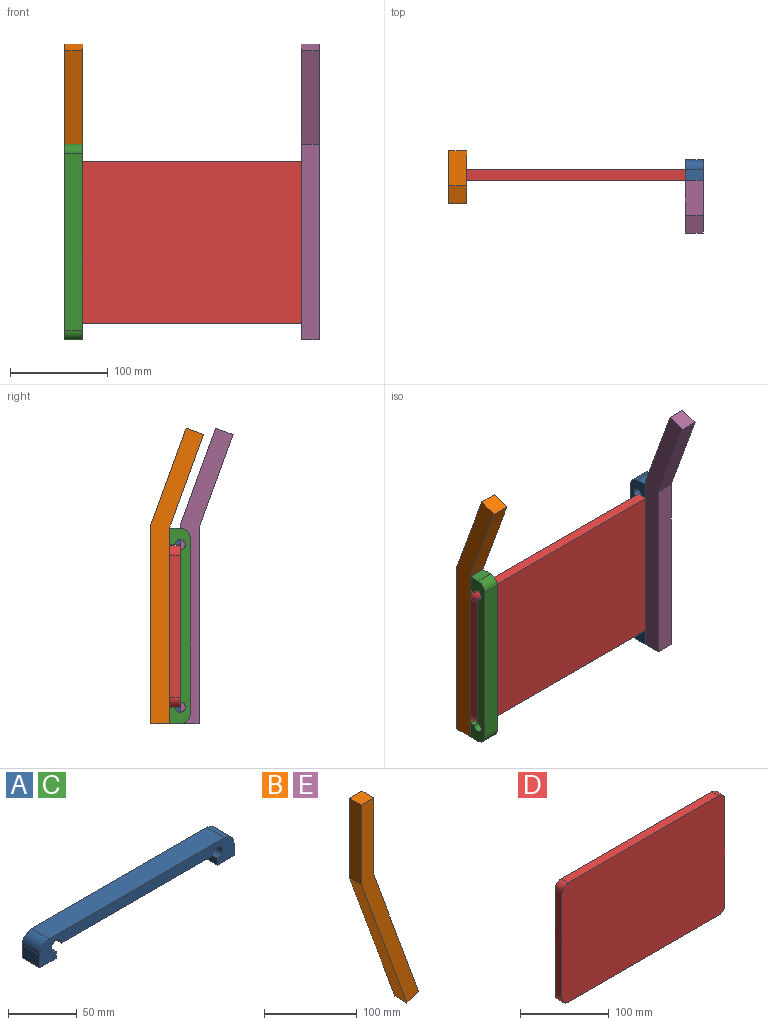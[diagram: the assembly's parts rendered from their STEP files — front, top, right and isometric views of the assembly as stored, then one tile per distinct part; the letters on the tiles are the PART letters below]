
ASSEMBLY  parts=5 mates=12
PART A: 14 faces, bbox 200x18.2x21 mm
  f0: plane 18.21x5.92mm, normal (1,0,0), area 107.8mm2, adj f6,f8,f9,f11
  f1: plane 155.84x18.21mm, normal (0,0,-1), area 2838.1mm2, adj f8,f9,f10,f11
  f2: plane 18.21x5.92mm, normal (-1,0,0), area 107.8mm2, adj f7,f8,f9,f10
  f3: plane 18.21x11.19mm, normal (1,0,0), area 203.8mm2, adj f7,f8,f9,f12
  f4: plane 180.38x18.21mm, normal (0,0,1), area 3285mm2, adj f8,f9,f12,f13
  f5: plane 18.21x11.19mm, normal (-1,0,0), area 203.8mm2, adj f6,f8,f9,f13
  f6: plane 18.21x17mm, normal (0,0,-1), area 309.6mm2, adj f0,f5,f8,f9
  f7: plane 18.21x17mm, normal (0,0,-1), area 309.6mm2, adj f2,f3,f8,f9
  f8: plane 200x21mm, normal (0,-1,0), area 2211.1mm2, adj f0,f1,f2,f3,f4,f5,f6,f7
  f9: plane 200x21mm, normal (0,1,0), area 2211.1mm2, adj f0,f1,f2,f3,f4,f5,f6,f7
  f10: cylinder r=5.08mm len=18.21mm, axis (0,-1,0), area 436mm2, adj f1,f2,f8,f9
  f11: cylinder r=5.08mm len=18.21mm, axis (0,-1,0), area 436mm2, adj f0,f1,f8,f9
  f12: cylinder r=9.81mm len=18.21mm, axis (0,1,0), area 280.7mm2, adj f3,f4,f8,f9
  f13: cylinder r=9.81mm len=18.21mm, axis (0,1,0), area 280.7mm2, adj f4,f5,f8,f9
PART B: 8 faces, bbox 87.5x18.2x296.1 mm
  f0: plane 187.94x68.4mm, normal (0.94,0,0.34), area 3642.4mm2, adj f1,f5,f6,f7
  f1: plane 101.6x18.21mm, normal (1,0,0), area 1850.3mm2, adj f0,f2,f6,f7
  f2: plane 19.05x18.21mm, normal (0,0,1), area 346.9mm2, adj f1,f3,f6,f7
  f3: plane 104.96x18.21mm, normal (-1,0,0), area 1911.5mm2, adj f2,f4,f6,f7
  f4: plane 191.1x69.55mm, normal (-0.94,0,-0.34), area 3703.5mm2, adj f3,f5,f6,f7
  f5: plane 18.21x17.9mm, normal (0.34,0,-0.94), area 346.9mm2, adj f0,f4,f6,f7
  f6: plane 296.05x87.45mm, normal (0,-1,0), area 5809.5mm2, adj f0,f1,f2,f3,f4,f5
  f7: plane 296.05x87.45mm, normal (0,1,0), area 5809.5mm2, adj f0,f1,f2,f3,f4,f5
PART C: same geometry as A
PART D: 10 faces, bbox 260x11.1x165 mm
  f0: plane 240x11.1mm, normal (0,0,-1), area 2664mm2, adj f4,f5,f6,f9
  f1: plane 145x11.1mm, normal (1,0,0), area 1609.5mm2, adj f4,f5,f6,f7
  f2: plane 240x11.1mm, normal (0,0,1), area 2664mm2, adj f4,f5,f7,f8
  f3: plane 145x11.1mm, normal (-1,0,0), area 1609.5mm2, adj f4,f5,f8,f9
  f4: plane 260x165mm, normal (0,-1,0), area 42814.2mm2, adj f0,f1,f2,f3,f6,f7,f8,f9
  f5: plane 260x165mm, normal (0,1,0), area 42814.2mm2, adj f0,f1,f2,f3,f6,f7,f8,f9
  f6: cylinder r=10mm len=11.1mm, axis (0,-1,0), area 174.4mm2, adj f0,f1,f4,f5
  f7: cylinder r=10mm len=11.1mm, axis (0,1,0), area 174.4mm2, adj f1,f2,f4,f5
  f8: cylinder r=10mm len=11.1mm, axis (0,-1,0), area 174.4mm2, adj f2,f3,f4,f5
  f9: cylinder r=10mm len=11.1mm, axis (0,1,0), area 174.4mm2, adj f0,f3,f4,f5
PART E: same geometry as B
PLACE A rot(axis=(-0.58,0.58,0.58),120deg) t=(36.92,-12.77,119.58)mm
PLACE B rot(axis=(0.17,0.17,-0.97),91.7deg) t=(-186.66,-12.67,136.58)mm
PLACE C rot(axis=(0.58,-0.58,0.58),120deg) t=(-204.87,-23.67,-46.42)mm
PLACE D t=(-74.87,-12.67,36.08)mm fixed
PLACE E rot(axis=(0.17,0.17,-0.97),91.7deg) t=(55.13,-42.82,136.58)mm
MATE planar B.f0 <-> D.f5  axis (0,-1,0) through (-195.76,-12.67,36.58)mm
MATE planar B.f0 <-> C.f6  axis (0,-1,0) through (-195.76,-12.67,-63.42)mm
MATE planar C.f0 <-> D.f0  axis (0,0,1) through (-195.76,-15.63,-46.42)mm
MATE planar D.f1 <-> E.f7  axis (1,0,0) through (55.13,-18.22,36.08)mm
MATE planar D.f3 <-> B.f6  axis (-1,0,0) through (-204.87,-18.22,36.08)mm
MATE planar A.f3 <-> E.f5  axis (0,0,-1) through (46.02,-18.18,-63.42)mm
MATE planar E.f4 <-> D.f4  axis (0,1,0) through (46.02,-23.77,38.26)mm
MATE planar C.f5 <-> B.f5  axis (0,0,-1) through (-195.76,-18.26,-63.42)mm
MATE planar A.f2 <-> D.f0  axis (0,0,1) through (46.02,-20.81,-46.42)mm
MATE planar C.f9 <-> B.f6  axis (-1,0,0) through (-204.87,-27.08,36.58)mm
MATE planar A.f7 <-> E.f4  axis (0,-1,0) through (46.02,-23.77,-54.92)mm
MATE planar A.f9 <-> E.f6  axis (-1,0,0) through (36.92,-9.36,36.58)mm
